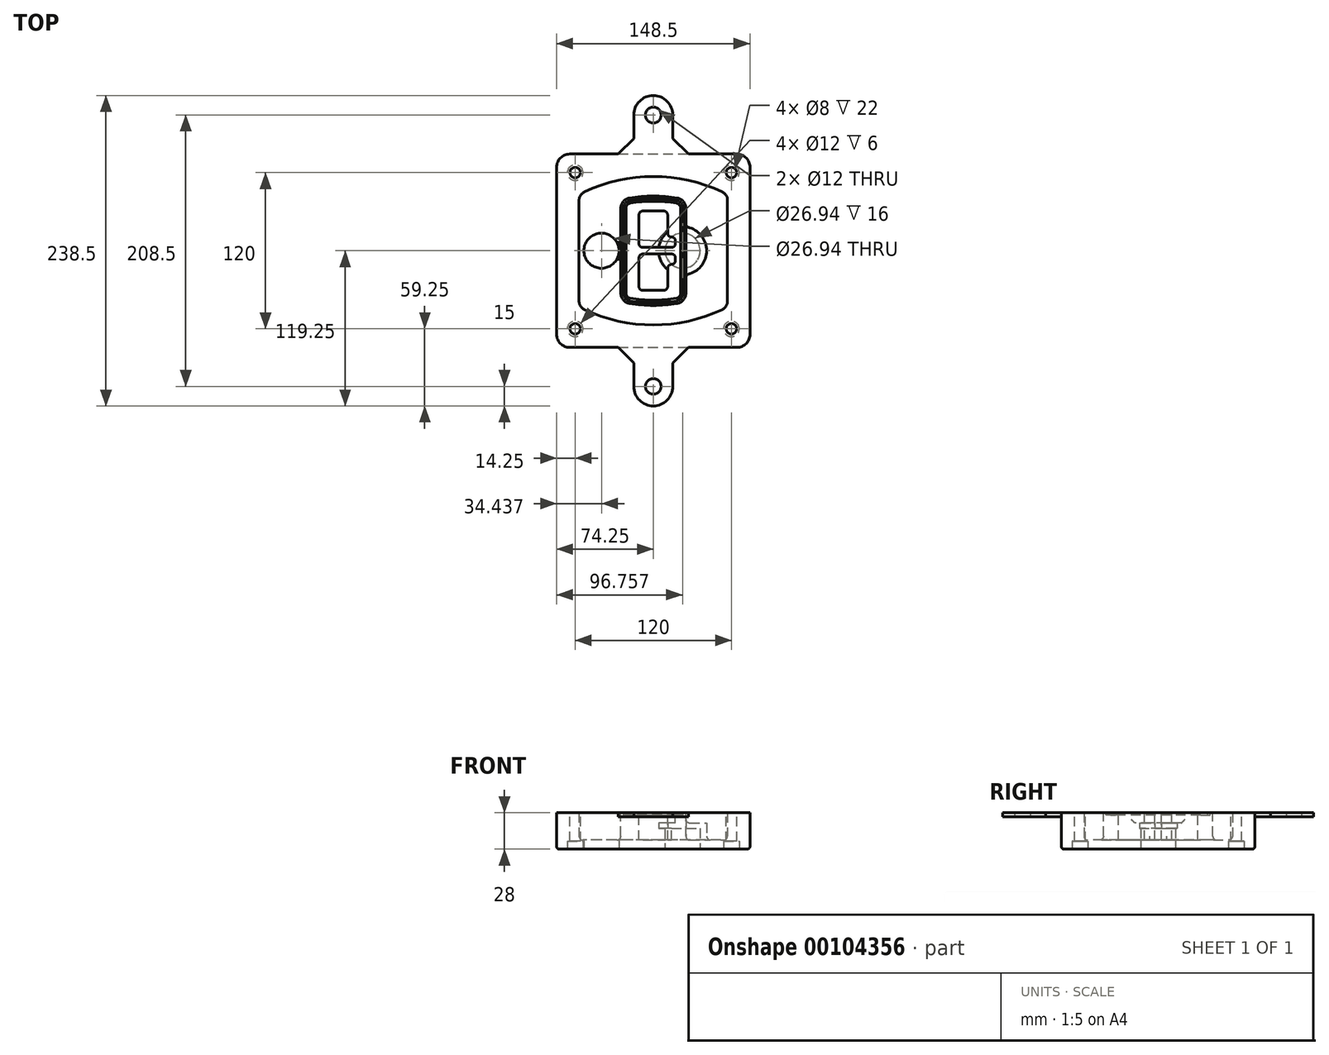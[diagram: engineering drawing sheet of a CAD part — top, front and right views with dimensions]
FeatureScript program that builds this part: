
annotation { "Feature Type Name" : "Feature", "Feature Type Description" : "" }
export const myFeature = defineFeature(function(context is Context, id is Id, definition is map)
    precondition{}
    {
        {
            var Q0;
            Q0=qCreatedBy(makeId("Top.planeOp"),FACE);
            var sketch = newSketch(context, id + "F0", { "sketchPlane" : qUnion([Q0])});
            skPoint(sketch, "E0.rect.middle", {"position": v(0, 0) * mm});
            skLineSegment(sketch, "E1.bottom", {"start": v(-64.25, -74.25) * mm, "end": v(64.25, -74.25) * mm});
            skLineSegment(sketch, "E1.top", {"start": v(-64.25, 74.25) * mm, "end": v(64.25, 74.25) * mm});
            skLineSegment(sketch, "E1.left", {"start": v(-74.25, -64.25) * mm, "end": v(-74.25, 64.25) * mm});
            skLineSegment(sketch, "E1.right", {"start": v(74.25, -64.25) * mm, "end": v(74.25, 64.25) * mm});
            skLineSegment(sketch, "E2", {"start": v(-74.25, 74.25) * mm, "end": v(74.25, -74.25) * mm, "construction": true});
            skLineSegment(sketch, "E3", {"start": v(74.25, 74.25) * mm, "end": v(-74.25, -74.25) * mm, "construction": true});
            skCircle(sketch, "E4", {"center": v(-60, 60) * mm, "radius": 4 * mm});
            skCircle(sketch, "E5", {"center": v(60, 60) * mm, "radius": 4 * mm});
            skCircle(sketch, "E6", {"center": v(60, -60) * mm, "radius": 4 * mm});
            skCircle(sketch, "E7", {"center": v(-60, -60) * mm, "radius": 4 * mm});
            skLineSegment(sketch, "E8", {"start": v(-60, 60) * mm, "end": v(60, 60) * mm, "construction": true});
            skLineSegment(sketch, "E9", {"start": v(60, 60) * mm, "end": v(60, -60) * mm, "construction": true});
            skLineSegment(sketch, "E10", {"start": v(60, -60) * mm, "end": v(-60, -60) * mm, "construction": true});
            skLineSegment(sketch, "E11", {"start": v(-60, -60) * mm, "end": v(-60, 60) * mm, "construction": true});
            skLineSegment(sketch, "E12", {"start": v(-60, 38.83) * mm, "end": v(-60, -38.83) * mm});
            skLineSegment(sketch, "E13", {"start": v(60, 38.83) * mm, "end": v(60, -38.83) * mm});
            skArc(sketch, "E14", {"start": v(54.26, 47.88) * mm, "mid": v(0, 60) * mm, "end": v(-54.26, 47.88) * mm});
            skArc(sketch, "E15", {"start": v(-54.26, -47.88) * mm, "mid": v(0, -60) * mm, "end": v(54.26, -47.88) * mm});
            skLineSegment(sketch, "E16", {"start": v(-60, 0) * mm, "end": v(60, 0) * mm, "construction": true});
            skPoint(sketch, "E17.visualSharp", {"position": v(-60, -45) * mm});
            skArc(sketch, "E17.filletArc", {"start": v(-60, -38.83) * mm, "mid": v(-58.44, -44.2) * mm, "end": v(-54.26, -47.88) * mm});
            skPoint(sketch, "E18.visualSharp", {"position": v(-60, 45) * mm});
            skArc(sketch, "E18.filletArc", {"start": v(-54.26, 47.88) * mm, "mid": v(-58.44, 44.2) * mm, "end": v(-60, 38.83) * mm});
            skPoint(sketch, "E19.visualSharp", {"position": v(60, 45) * mm});
            skArc(sketch, "E19.filletArc", {"start": v(60, 38.83) * mm, "mid": v(58.44, 44.2) * mm, "end": v(54.26, 47.88) * mm});
            skPoint(sketch, "E20.visualSharp", {"position": v(60, -45) * mm});
            skArc(sketch, "E20.filletArc", {"start": v(54.26, -47.88) * mm, "mid": v(58.44, -44.2) * mm, "end": v(60, -38.83) * mm});
            skPoint(sketch, "E21.visualSharp", {"position": v(-74.25, 74.25) * mm});
            skArc(sketch, "E21.filletArc", {"start": v(-64.25, 74.25) * mm, "mid": v(-71.32, 71.32) * mm, "end": v(-74.25, 64.25) * mm});
            skPoint(sketch, "E22.visualSharp", {"position": v(74.25, 74.25) * mm});
            skArc(sketch, "E22.filletArc", {"start": v(74.25, 64.25) * mm, "mid": v(71.32, 71.32) * mm, "end": v(64.25, 74.25) * mm});
            skPoint(sketch, "E23.visualSharp", {"position": v(74.25, -74.25) * mm});
            skArc(sketch, "E23.filletArc", {"start": v(64.25, -74.25) * mm, "mid": v(71.32, -71.32) * mm, "end": v(74.25, -64.25) * mm});
            skPoint(sketch, "E24.visualSharp", {"position": v(-74.25, -74.25) * mm});
            skArc(sketch, "E24.filletArc", {"start": v(-74.25, -64.25) * mm, "mid": v(-71.32, -71.32) * mm, "end": v(-64.25, -74.25) * mm});
            skArc(sketch, "E25.0", {"start": v(57, 38.83) * mm, "mid": v(55.9, 42.58) * mm, "end": v(52.98, 45.17) * mm});
            skLineSegment(sketch, "E25.1", {"start": v(57, 38.83) * mm, "end": v(57, -38.83) * mm});
            skArc(sketch, "E25.2", {"start": v(52.98, -45.17) * mm, "mid": v(55.9, -42.58) * mm, "end": v(57, -38.83) * mm});
            skArc(sketch, "E25.3", {"start": v(-52.98, -45.17) * mm, "mid": v(0, -57) * mm, "end": v(52.98, -45.17) * mm});
            skArc(sketch, "E25.4", {"start": v(-57, -38.83) * mm, "mid": v(-55.9, -42.58) * mm, "end": v(-52.98, -45.17) * mm});
            skArc(sketch, "E25.5", {"start": v(52.98, 45.17) * mm, "mid": v(0, 57) * mm, "end": v(-52.98, 45.17) * mm});
            skLineSegment(sketch, "E25.6", {"start": v(-57, 38.83) * mm, "end": v(-57, -38.83) * mm});
            skArc(sketch, "E25.7", {"start": v(-52.98, 45.17) * mm, "mid": v(-55.9, 42.58) * mm, "end": v(-57, 38.83) * mm});
            skArc(sketch, "E26.0", {"start": v(-55.96, 51.5) * mm, "mid": v(-61.82, 46.33) * mm, "end": v(-64, 38.83) * mm});
            skArc(sketch, "E26.1", {"start": v(55.96, 51.5) * mm, "mid": v(0, 64) * mm, "end": v(-55.96, 51.5) * mm});
            skArc(sketch, "E26.2", {"start": v(64, 38.83) * mm, "mid": v(61.82, 46.33) * mm, "end": v(55.96, 51.5) * mm});
            skLineSegment(sketch, "E26.3", {"start": v(64, 38.83) * mm, "end": v(64, -38.83) * mm});
            skArc(sketch, "E26.4", {"start": v(55.96, -51.5) * mm, "mid": v(61.82, -46.33) * mm, "end": v(64, -38.83) * mm});
            skLineSegment(sketch, "E26.5", {"start": v(-64, 38.83) * mm, "end": v(-64, -38.83) * mm});
            skArc(sketch, "E26.6", {"start": v(-55.96, -51.5) * mm, "mid": v(0, -64) * mm, "end": v(55.96, -51.5) * mm});
            skArc(sketch, "E26.7", {"start": v(-64, -38.83) * mm, "mid": v(-61.82, -46.33) * mm, "end": v(-55.96, -51.5) * mm});
            skSolve(sketch);
        }
        {
            var Q0;
            Q0=makeQuery(id+"F0.imprint","IMPRINT",FACE,{"disambiguationData":[TD([[makeQuery(id+"F0.imprint","IMPRINT",EDGE,{"derivedFrom":sQuery(id+"F0.wireOp",EDGE,"E1.bottom")}),1.0]])]});
            var Q1;
            Q1=makeQuery(id+"F0.imprint","IMPRINT",FACE,{"disambiguationData":[TD([[makeQuery(id+"F0.imprint","IMPRINT",EDGE,{"derivedFrom":sQuery(id+"F0.wireOp",EDGE,"E12")}),1.0]])]});
            var Q2;
            Q2=makeQuery(id+"F0.imprint","IMPRINT",FACE,{"disambiguationData":[TD([[makeQuery(id+"F0.imprint","IMPRINT",EDGE,{"derivedFrom":sQuery(id+"F0.wireOp",EDGE,"E25.0")}),1.0]])]});
            var Q3;
            Q3=makeQuery(id+"F0.imprint","IMPRINT",FACE,{"disambiguationData":[TD([[makeQuery(id+"F0.imprint","IMPRINT",EDGE,{"derivedFrom":sQuery(id+"F0.wireOp",EDGE,"E12")}),-1.0]])]});
            extrude(context, id + "F1", {"entities" : qUnion([Q0, Q1, Q2, Q3]), "oppositeDirection" : true, "depth" : 25 * mm});
        }
        {
            var Q0;
            Q0=makeQuery(id+"F0.imprint","IMPRINT",FACE,{"disambiguationData":[TD([[makeQuery(id+"F0.imprint","IMPRINT",EDGE,{"derivedFrom":sQuery(id+"F0.wireOp",EDGE,"E12")}),1.0]])]});
            extrude(context, id + "F2", {"entities" : qUnion([Q0]), "operationType" : NewBodyOperationType.ADD, "depth" : 3 * mm});
        }
        {
            var Q0;
            Q0=makeQuery(id+"F0.imprint","IMPRINT",FACE,{"disambiguationData":[TD([[makeQuery(id+"F0.imprint","IMPRINT",EDGE,{"derivedFrom":sQuery(id+"F0.wireOp",EDGE,"E25.0")}),1.0]])]});
            extrude(context, id + "F3", {"entities" : qUnion([Q0]), "operationType" : NewBodyOperationType.REMOVE, "oppositeDirection" : true, "depth" : 18 * mm});
        }
        {
            var Q0;
            Q0=makeQuery(id+"F2.opExtrude","CAP_FACE",FACE,{"disambiguationData":[OSD([sQuery(id+"F0.wireOp",EDGE,"E12"),sQuery(id+"F0.wireOp",EDGE,"E13"),sQuery(id+"F0.wireOp",EDGE,"E14"),sQuery(id+"F0.wireOp",EDGE,"E15"),sQuery(id+"F0.wireOp",EDGE,"E17.filletArc"),sQuery(id+"F0.wireOp",EDGE,"E18.filletArc"),sQuery(id+"F0.wireOp",EDGE,"E19.filletArc"),sQuery(id+"F0.wireOp",EDGE,"E20.filletArc"),sQuery(id+"F0.wireOp",EDGE,"E25.0"),sQuery(id+"F0.wireOp",EDGE,"E25.1"),sQuery(id+"F0.wireOp",EDGE,"E25.2"),sQuery(id+"F0.wireOp",EDGE,"E25.3"),sQuery(id+"F0.wireOp",EDGE,"E25.4"),sQuery(id+"F0.wireOp",EDGE,"E25.5"),sQuery(id+"F0.wireOp",EDGE,"E25.6"),sQuery(id+"F0.wireOp",EDGE,"E25.7")])],"isStart":false});
            var sketch = newSketch(context, id + "F4", { "sketchPlane" : qUnion([Q0])});
            skArc(sketch, "E27.0", {"start": v(-18.34, -40.45) * mm, "mid": v(0, -42) * mm, "end": v(18.34, -40.45) * mm});
            skArc(sketch, "E28.0", {"start": v(18.34, 40.45) * mm, "mid": v(0, 42) * mm, "end": v(-18.34, 40.45) * mm});
            skLineSegment(sketch, "E29", {"start": v(-25, 32.57) * mm, "end": v(-25, -32.57) * mm});
            skLineSegment(sketch, "E30", {"start": v(25, 32.57) * mm, "end": v(25, -32.57) * mm});
            skLineSegment(sketch, "E31", {"start": v(-25, 39.1) * mm, "end": v(25, 39.1) * mm, "construction": true});
            skLineSegment(sketch, "E32", {"start": v(-25, -39.1) * mm, "end": v(25, -39.1) * mm, "construction": true});
            skPoint(sketch, "E33.visualSharp", {"position": v(-25, 39.1) * mm});
            skArc(sketch, "E33.filletArc", {"start": v(-18.34, 40.45) * mm, "mid": v(-23.11, 37.73) * mm, "end": v(-25, 32.57) * mm});
            skPoint(sketch, "E34.visualSharp", {"position": v(25, 39.1) * mm});
            skArc(sketch, "E34.filletArc", {"start": v(25, 32.57) * mm, "mid": v(23.11, 37.73) * mm, "end": v(18.34, 40.45) * mm});
            skPoint(sketch, "E35.visualSharp", {"position": v(25, -39.1) * mm});
            skArc(sketch, "E35.filletArc", {"start": v(18.34, -40.45) * mm, "mid": v(23.11, -37.73) * mm, "end": v(25, -32.57) * mm});
            skPoint(sketch, "E36.visualSharp", {"position": v(-25, -39.1) * mm});
            skArc(sketch, "E36.filletArc", {"start": v(-25, -32.57) * mm, "mid": v(-23.11, -37.73) * mm, "end": v(-18.34, -40.45) * mm});
            skArc(sketch, "E37.0", {"start": v(52.98, 45.17) * mm, "mid": v(0, 57) * mm, "end": v(-52.98, 45.17) * mm});
            skArc(sketch, "E37.1", {"start": v(-52.98, 45.17) * mm, "mid": v(-55.9, 42.58) * mm, "end": v(-57, 38.83) * mm});
            skLineSegment(sketch, "E37.2", {"start": v(-57, 38.83) * mm, "end": v(-57, -38.83) * mm});
            skArc(sketch, "E37.3", {"start": v(-57, -38.83) * mm, "mid": v(-55.9, -42.58) * mm, "end": v(-52.98, -45.17) * mm});
            skArc(sketch, "E37.4", {"start": v(-52.98, -45.17) * mm, "mid": v(0, -57) * mm, "end": v(52.98, -45.17) * mm});
            skArc(sketch, "E37.5", {"start": v(52.98, -45.17) * mm, "mid": v(55.9, -42.58) * mm, "end": v(57, -38.83) * mm});
            skLineSegment(sketch, "E37.6", {"start": v(57, 38.83) * mm, "end": v(57, -38.83) * mm});
            skArc(sketch, "E37.7", {"start": v(57, 38.83) * mm, "mid": v(55.9, 42.58) * mm, "end": v(52.98, 45.17) * mm});
            skLineSegment(sketch, "E38.0", {"start": v(23, 32.57) * mm, "end": v(23, -32.57) * mm});
            skArc(sketch, "E38.1", {"start": v(18, -38.48) * mm, "mid": v(21.58, -36.44) * mm, "end": v(23, -32.57) * mm});
            skArc(sketch, "E38.2", {"start": v(-18, -38.48) * mm, "mid": v(0, -40) * mm, "end": v(18, -38.48) * mm});
            skArc(sketch, "E38.3", {"start": v(-23, -32.57) * mm, "mid": v(-21.58, -36.44) * mm, "end": v(-18, -38.48) * mm});
            skLineSegment(sketch, "E38.4", {"start": v(-23, 32.57) * mm, "end": v(-23, -32.57) * mm});
            skArc(sketch, "E38.5", {"start": v(23, 32.57) * mm, "mid": v(21.58, 36.44) * mm, "end": v(18, 38.48) * mm});
            skArc(sketch, "E38.6", {"start": v(-18, 38.48) * mm, "mid": v(-21.58, 36.44) * mm, "end": v(-23, 32.57) * mm});
            skArc(sketch, "E38.7", {"start": v(18, 38.48) * mm, "mid": v(0, 40) * mm, "end": v(-18, 38.48) * mm});
            skArc(sketch, "E39.0", {"start": v(21, 32.57) * mm, "mid": v(20.06, 35.15) * mm, "end": v(17.67, 36.5) * mm});
            skLineSegment(sketch, "E39.1", {"start": v(21, 32.57) * mm, "end": v(21, -32.57) * mm});
            skArc(sketch, "E39.2", {"start": v(17.67, -36.5) * mm, "mid": v(20.06, -35.15) * mm, "end": v(21, -32.57) * mm});
            skArc(sketch, "E39.3", {"start": v(-17.67, -36.5) * mm, "mid": v(0, -38) * mm, "end": v(17.67, -36.5) * mm});
            skArc(sketch, "E39.4", {"start": v(-21, -32.57) * mm, "mid": v(-20.06, -35.15) * mm, "end": v(-17.67, -36.5) * mm});
            skArc(sketch, "E39.5", {"start": v(17.67, 36.5) * mm, "mid": v(0, 38) * mm, "end": v(-17.67, 36.5) * mm});
            skLineSegment(sketch, "E39.6", {"start": v(-21, 32.57) * mm, "end": v(-21, -32.57) * mm});
            skArc(sketch, "E39.7", {"start": v(-17.67, 36.5) * mm, "mid": v(-20.06, 35.15) * mm, "end": v(-21, 32.57) * mm});
            skLineSegment(sketch, "E40", {"start": v(-25, 0) * mm, "end": v(25, 0) * mm, "construction": true});
            skLineSegment(sketch, "E41", {"start": v(-11, 5.5) * mm, "end": v(-11, 27.5) * mm});
            skLineSegment(sketch, "E42", {"start": v(-8, 30.5) * mm, "end": v(8, 30.5) * mm});
            skLineSegment(sketch, "E43", {"start": v(11, 27.5) * mm, "end": v(11, 13.5) * mm});
            skLineSegment(sketch, "E44", {"start": v(14, 10.5) * mm, "end": v(14, 10.5) * mm});
            skLineSegment(sketch, "E45", {"start": v(17, 7.5) * mm, "end": v(17, 5.5) * mm});
            skLineSegment(sketch, "E46", {"start": v(14, 2.5) * mm, "end": v(-8, 2.5) * mm});
            skPoint(sketch, "E47.visualSharp", {"position": v(-11, 30.5) * mm});
            skArc(sketch, "E47.filletArc", {"start": v(-8, 30.5) * mm, "mid": v(-10.12, 29.62) * mm, "end": v(-11, 27.5) * mm});
            skPoint(sketch, "E48.visualSharp", {"position": v(11, 30.5) * mm});
            skArc(sketch, "E48.filletArc", {"start": v(11, 27.5) * mm, "mid": v(10.12, 29.62) * mm, "end": v(8, 30.5) * mm});
            skPoint(sketch, "E49.visualSharp", {"position": v(11, 10.5) * mm});
            skArc(sketch, "E49.filletArc", {"start": v(11, 13.5) * mm, "mid": v(11.88, 11.38) * mm, "end": v(14, 10.5) * mm});
            skPoint(sketch, "E50.visualSharp", {"position": v(17, 10.5) * mm});
            skArc(sketch, "E50.filletArc", {"start": v(17, 7.5) * mm, "mid": v(16.12, 9.62) * mm, "end": v(14, 10.5) * mm});
            skPoint(sketch, "E51.visualSharp", {"position": v(17, 2.5) * mm});
            skArc(sketch, "E51.filletArc", {"start": v(14, 2.5) * mm, "mid": v(16.12, 3.38) * mm, "end": v(17, 5.5) * mm});
            skPoint(sketch, "E52.visualSharp", {"position": v(-11, 2.5) * mm});
            skArc(sketch, "E52.filletArc", {"start": v(-11, 5.5) * mm, "mid": v(-10.12, 3.38) * mm, "end": v(-8, 2.5) * mm});
            skLineSegment(sketch, "E53.0.MirrorCS", {"start": v(14, -2.5) * mm, "end": v(-8, -2.5) * mm});
            skArc(sketch, "E54.0.MirrorCS", {"start": v(-11, -5.5) * mm, "mid": v(-10.12, -3.38) * mm, "end": v(-8, -2.5) * mm});
            skLineSegment(sketch, "E55.0.MirrorCS", {"start": v(-11, -5.5) * mm, "end": v(-11, -27.5) * mm});
            skArc(sketch, "E56.0.MirrorCS", {"start": v(-8, -30.5) * mm, "mid": v(-10.12, -29.62) * mm, "end": v(-11, -27.5) * mm});
            skLineSegment(sketch, "E57.0.MirrorCS", {"start": v(-8, -30.5) * mm, "end": v(8, -30.5) * mm});
            skArc(sketch, "E58.0.MirrorCS", {"start": v(11, -27.5) * mm, "mid": v(10.12, -29.62) * mm, "end": v(8, -30.5) * mm});
            skLineSegment(sketch, "E59.0.MirrorCS", {"start": v(11, -27.5) * mm, "end": v(11, -13.5) * mm});
            skArc(sketch, "E60.0.MirrorCS", {"start": v(11, -13.5) * mm, "mid": v(11.88, -11.38) * mm, "end": v(14, -10.5) * mm});
            skArc(sketch, "E61.0.MirrorCS", {"start": v(17, -7.5) * mm, "mid": v(16.12, -9.62) * mm, "end": v(14, -10.5) * mm});
            skLineSegment(sketch, "E62.0.MirrorCS", {"start": v(17, -7.5) * mm, "end": v(17, -5.5) * mm});
            skArc(sketch, "E63.0.MirrorCS", {"start": v(14, -2.5) * mm, "mid": v(16.12, -3.38) * mm, "end": v(17, -5.5) * mm});
            skSolve(sketch);
        }
        {
            var Q0;
            Q0=makeQuery(id+"F4.imprint","IMPRINT",FACE,{"disambiguationData":[TD([[makeQuery(id+"F4.imprint","IMPRINT",EDGE,{"derivedFrom":sQuery(id+"F4.wireOp",EDGE,"E27.0")}),1.0]])]});
            var Q1;
            Q1=makeQuery(id+"F4.imprint","IMPRINT",FACE,{"disambiguationData":[TD([[makeQuery(id+"F4.imprint","IMPRINT",EDGE,{"derivedFrom":sQuery(id+"F4.wireOp",EDGE,"E38.0")}),-1.0]])]});
            var Q2;
            Q2=makeQuery(id+"F4.imprint","IMPRINT",FACE,{"disambiguationData":[TD([[makeQuery(id+"F4.imprint","IMPRINT",EDGE,{"derivedFrom":sQuery(id+"F4.wireOp",EDGE,"E39.0")}),1.0]])]});
            extrude(context, id + "F5", {"entities" : qUnion([Q0, Q1, Q2]), "operationType" : NewBodyOperationType.ADD, "endBound" : BoundingType.UP_TO_NEXT, "oppositeDirection" : true, "depth" : 25 * mm});
        }
        {
            var Q0;
            Q0=makeQuery(id+"F4.imprint","IMPRINT",FACE,{"disambiguationData":[TD([[makeQuery(id+"F4.imprint","IMPRINT",EDGE,{"derivedFrom":sQuery(id+"F4.wireOp",EDGE,"E38.0")}),-1.0]])]});
            extrude(context, id + "F6", {"entities" : qUnion([Q0]), "operationType" : NewBodyOperationType.REMOVE, "oppositeDirection" : true, "depth" : 2 * mm});
        }
        {
            var Q0;
            Q0=makeQuery(id+"F1.opExtrude","CAP_FACE",FACE,{"disambiguationData":[OSD([sQuery(id+"F0.wireOp",EDGE,"E1.bottom"),sQuery(id+"F0.wireOp",EDGE,"E1.top"),sQuery(id+"F0.wireOp",EDGE,"E1.left"),sQuery(id+"F0.wireOp",EDGE,"E1.right"),sQuery(id+"F0.wireOp",EDGE,"E4"),sQuery(id+"F0.wireOp",EDGE,"E5"),sQuery(id+"F0.wireOp",EDGE,"E6"),sQuery(id+"F0.wireOp",EDGE,"E7"),sQuery(id+"F0.wireOp",EDGE,"E21.filletArc"),sQuery(id+"F0.wireOp",EDGE,"E22.filletArc"),sQuery(id+"F0.wireOp",EDGE,"E23.filletArc"),sQuery(id+"F0.wireOp",EDGE,"E24.filletArc")])],"isStart":false});
            var sketch = newSketch(context, id + "F7", { "sketchPlane" : qUnion([Q0])});
            skCircle(sketch, "E64", {"center": v(22.5, 0) * mm, "radius": 13.47 * mm});
            skCircle(sketch, "E65", {"center": v(-39.81, 0) * mm, "radius": 13.47 * mm});
            skLineSegment(sketch, "E66", {"start": v(74.25, 0) * mm, "end": v(-74.25, 0) * mm});
            skCircle(sketch, "E67", {"center": v(22.5, 0) * mm, "radius": 18.47 * mm});
            skCircle(sketch, "E68", {"center": v(60, -60) * mm, "radius": 6 * mm});
            skCircle(sketch, "E69", {"center": v(-60, -60) * mm, "radius": 6 * mm});
            skCircle(sketch, "E70", {"center": v(-60, 60) * mm, "radius": 6 * mm});
            skCircle(sketch, "E71", {"center": v(60, 60) * mm, "radius": 6 * mm});
            skSolve(sketch);
        }
        {
            var Q0;
            {var subQ1=sQuery(id+"F7.wireOp",EDGE,"E66");var subQ4=sQuery(id+"F7.wireOp",EDGE,"E64");var subQ6=makeQuery(id+"F7.imprint","INTERSECT",VERTEX,{"disambiguationData":[OD(0.0)],"derivedFrom":[subQ4,subQ1]});Q0=makeQuery(id+"F7.imprint","IMPRINT",FACE,{"disambiguationData":[TD([[makeQuery(id+"F7.imprint","IMPRINT",EDGE,{"disambiguationData":[TD([[subQ6,-1.0]])],"derivedFrom":subQ4}),-1.0]])]});}
            var Q1;
            {var subQ0=sQuery(id+"F7.wireOp",EDGE,"E66");var subQ1=sQuery(id+"F7.wireOp",EDGE,"E64");var subQ3=makeQuery(id+"F7.imprint","INTERSECT",VERTEX,{"disambiguationData":[OD(0.0)],"derivedFrom":[subQ1,subQ0]});Q1=makeQuery(id+"F7.imprint","IMPRINT",FACE,{"disambiguationData":[TD([[makeQuery(id+"F7.imprint","IMPRINT",EDGE,{"disambiguationData":[TD([[subQ3,-1.0]])],"derivedFrom":subQ1}),1.0]])]});}
            var Q2;
            {var subQ0=sQuery(id+"F7.wireOp",EDGE,"E66");var subQ1=sQuery(id+"F7.wireOp",EDGE,"E64");var subQ3=makeQuery(id+"F7.imprint","INTERSECT",VERTEX,{"disambiguationData":[OD(0.0)],"derivedFrom":[subQ1,subQ0]});Q2=makeQuery(id+"F7.imprint","IMPRINT",FACE,{"disambiguationData":[TD([[makeQuery(id+"F7.imprint","IMPRINT",EDGE,{"disambiguationData":[TD([[subQ3,1.0]])],"derivedFrom":subQ1}),1.0]])]});}
            var Q3;
            {var subQ1=sQuery(id+"F7.wireOp",EDGE,"E66");var subQ4=sQuery(id+"F7.wireOp",EDGE,"E64");var subQ6=makeQuery(id+"F7.imprint","INTERSECT",VERTEX,{"disambiguationData":[OD(0.0)],"derivedFrom":[subQ4,subQ1]});Q3=makeQuery(id+"F7.imprint","IMPRINT",FACE,{"disambiguationData":[TD([[makeQuery(id+"F7.imprint","IMPRINT",EDGE,{"disambiguationData":[TD([[subQ6,1.0]])],"derivedFrom":subQ4}),-1.0]])]});}
            extrude(context, id + "F8", {"entities" : qUnion([Q0, Q1, Q2, Q3]), "operationType" : NewBodyOperationType.ADD, "oppositeDirection" : true, "depth" : 20 * mm});
        }
        {
            var Q0;
            {var subQ0=sQuery(id+"F7.wireOp",EDGE,"E66");var subQ1=sQuery(id+"F7.wireOp",EDGE,"E64");var subQ3=makeQuery(id+"F7.imprint","INTERSECT",VERTEX,{"disambiguationData":[OD(0.0)],"derivedFrom":[subQ1,subQ0]});Q0=makeQuery(id+"F7.imprint","IMPRINT",FACE,{"disambiguationData":[TD([[makeQuery(id+"F7.imprint","IMPRINT",EDGE,{"disambiguationData":[TD([[subQ3,-1.0]])],"derivedFrom":subQ1}),1.0]])]});}
            var Q1;
            {var subQ0=sQuery(id+"F7.wireOp",EDGE,"E66");var subQ1=sQuery(id+"F7.wireOp",EDGE,"E64");var subQ3=makeQuery(id+"F7.imprint","INTERSECT",VERTEX,{"disambiguationData":[OD(0.0)],"derivedFrom":[subQ1,subQ0]});Q1=makeQuery(id+"F7.imprint","IMPRINT",FACE,{"disambiguationData":[TD([[makeQuery(id+"F7.imprint","IMPRINT",EDGE,{"disambiguationData":[TD([[subQ3,1.0]])],"derivedFrom":subQ1}),1.0]])]});}
            extrude(context, id + "F9", {"entities" : qUnion([Q0, Q1]), "operationType" : NewBodyOperationType.REMOVE, "oppositeDirection" : true, "depth" : 16 * mm});
        }
        {
            var Q0;
            {var subQ0=sQuery(id+"F7.wireOp",EDGE,"E66");var subQ1=sQuery(id+"F7.wireOp",EDGE,"E65");var subQ3=makeQuery(id+"F7.imprint","INTERSECT",VERTEX,{"disambiguationData":[OD(0.0)],"derivedFrom":[subQ1,subQ0]});Q0=makeQuery(id+"F7.imprint","IMPRINT",FACE,{"disambiguationData":[TD([[makeQuery(id+"F7.imprint","IMPRINT",EDGE,{"disambiguationData":[TD([[subQ3,-1.0]])],"derivedFrom":subQ1}),1.0]])]});}
            var Q1;
            {var subQ0=sQuery(id+"F7.wireOp",EDGE,"E66");var subQ1=sQuery(id+"F7.wireOp",EDGE,"E65");var subQ3=makeQuery(id+"F7.imprint","INTERSECT",VERTEX,{"disambiguationData":[OD(0.0)],"derivedFrom":[subQ1,subQ0]});Q1=makeQuery(id+"F7.imprint","IMPRINT",FACE,{"disambiguationData":[TD([[makeQuery(id+"F7.imprint","IMPRINT",EDGE,{"disambiguationData":[TD([[subQ3,1.0]])],"derivedFrom":subQ1}),1.0]])]});}
            extrude(context, id + "F10", {"entities" : qUnion([Q0, Q1]), "operationType" : NewBodyOperationType.REMOVE, "oppositeDirection" : true, "depth" : 25 * mm});
        }
        {
            var Q0;
            Q0=makeQuery(id+"F7.imprint","IMPRINT",FACE,{"disambiguationData":[TD([[makeQuery(id+"F7.imprint","IMPRINT",EDGE,{"derivedFrom":sQuery(id+"F7.wireOp",EDGE,"E68")}),1.0]])]});
            var Q1;
            Q1=makeQuery(id+"F7.imprint","IMPRINT",FACE,{"disambiguationData":[TD([[makeQuery(id+"F7.imprint","IMPRINT",EDGE,{"derivedFrom":makeQuery(id+"F1.opExtrude","CAP_EDGE",EDGE,{"disambiguationData":[OSD([sQuery(id+"F0.wireOp",EDGE,"E5")])],"isStart":false})}),-1.0]])]});
            var Q2;
            Q2=makeQuery(id+"F7.imprint","IMPRINT",FACE,{"disambiguationData":[TD([[makeQuery(id+"F7.imprint","IMPRINT",EDGE,{"derivedFrom":sQuery(id+"F7.wireOp",EDGE,"E69")}),1.0]])]});
            var Q3;
            Q3=makeQuery(id+"F7.imprint","IMPRINT",FACE,{"disambiguationData":[TD([[makeQuery(id+"F7.imprint","IMPRINT",EDGE,{"derivedFrom":makeQuery(id+"F1.opExtrude","CAP_EDGE",EDGE,{"disambiguationData":[OSD([sQuery(id+"F0.wireOp",EDGE,"E4")])],"isStart":false})}),-1.0]])]});
            var Q4;
            Q4=makeQuery(id+"F7.imprint","IMPRINT",FACE,{"disambiguationData":[TD([[makeQuery(id+"F7.imprint","IMPRINT",EDGE,{"derivedFrom":sQuery(id+"F7.wireOp",EDGE,"E70")}),1.0]])]});
            var Q5;
            Q5=makeQuery(id+"F7.imprint","IMPRINT",FACE,{"disambiguationData":[TD([[makeQuery(id+"F7.imprint","IMPRINT",EDGE,{"derivedFrom":makeQuery(id+"F1.opExtrude","CAP_EDGE",EDGE,{"disambiguationData":[OSD([sQuery(id+"F0.wireOp",EDGE,"E7")])],"isStart":false})}),-1.0]])]});
            var Q6;
            Q6=makeQuery(id+"F7.imprint","IMPRINT",FACE,{"disambiguationData":[TD([[makeQuery(id+"F7.imprint","IMPRINT",EDGE,{"derivedFrom":sQuery(id+"F7.wireOp",EDGE,"E71")}),1.0]])]});
            var Q7;
            Q7=makeQuery(id+"F7.imprint","IMPRINT",FACE,{"disambiguationData":[TD([[makeQuery(id+"F7.imprint","IMPRINT",EDGE,{"derivedFrom":makeQuery(id+"F1.opExtrude","CAP_EDGE",EDGE,{"disambiguationData":[OSD([sQuery(id+"F0.wireOp",EDGE,"E6")])],"isStart":false})}),-1.0]])]});
            extrude(context, id + "F11", {"entities" : qUnion([Q0, Q1, Q2, Q3, Q4, Q5, Q6, Q7]), "operationType" : NewBodyOperationType.REMOVE, "oppositeDirection" : true, "depth" : 6 * mm});
        }
        {
            var Q0;
            Q0=makeQuery(id+"F9.boolean.opBoolean","COPY",FACE,{"derivedFrom":makeQuery(id+"F9.opExtrude","CAP_FACE",FACE,{"disambiguationData":[OSD([sQuery(id+"F7.wireOp",EDGE,"E64")])],"isStart":false})});
            var sketch = newSketch(context, id + "F12", { "sketchPlane" : qUnion([Q0])});
            skArc(sketch, "E72.0", {"start": v(11, 14.45) * mm, "mid": v(6.45, 9.13) * mm, "end": v(4.2, 2.5) * mm});
            skArc(sketch, "E72.1", {"start": v(4.2, -2.5) * mm, "mid": v(6.45, -9.13) * mm, "end": v(11, -14.45) * mm});
            skLineSegment(sketch, "E73", {"start": v(4.2, -2.5) * mm, "end": v(14, -2.5) * mm});
            skLineSegment(sketch, "E74.0", {"start": v(14, 2.5) * mm, "end": v(4.2, 2.5) * mm});
            skArc(sketch, "E74.1", {"start": v(14, 2.5) * mm, "mid": v(16.12, 3.38) * mm, "end": v(17, 5.5) * mm});
            skLineSegment(sketch, "E74.2", {"start": v(17, 7.5) * mm, "end": v(17, 5.5) * mm});
            skArc(sketch, "E74.3", {"start": v(17, 7.5) * mm, "mid": v(16.12, 9.62) * mm, "end": v(14, 10.5) * mm});
            skArc(sketch, "E74.4", {"start": v(11, 13.5) * mm, "mid": v(11.88, 11.38) * mm, "end": v(14, 10.5) * mm});
            skLineSegment(sketch, "E74.5", {"start": v(11, 14.45) * mm, "end": v(11, 13.5) * mm});
            skLineSegment(sketch, "E74.7", {"start": v(14, -2.5) * mm, "end": v(4.2, -2.5) * mm});
            skArc(sketch, "E74.8", {"start": v(14, -2.5) * mm, "mid": v(16.12, -3.38) * mm, "end": v(17, -5.5) * mm});
            skLineSegment(sketch, "E74.9", {"start": v(17, -7.5) * mm, "end": v(17, -5.5) * mm});
            skArc(sketch, "E74.10", {"start": v(17, -7.5) * mm, "mid": v(16.12, -9.62) * mm, "end": v(14, -10.5) * mm});
            skArc(sketch, "E74.11", {"start": v(11, -13.5) * mm, "mid": v(11.88, -11.38) * mm, "end": v(14, -10.5) * mm});
            skLineSegment(sketch, "E74.12", {"start": v(11, -14.45) * mm, "end": v(11, -13.5) * mm});
            skPoint(sketch, "E75.orphan", {"position": v(11, -27.5) * mm});
            skPoint(sketch, "E76.orphan", {"position": v(-8, -2.5) * mm});
            skPoint(sketch, "E77.orphan", {"position": v(-8, 2.5) * mm});
            skPoint(sketch, "E78.orphan", {"position": v(11, 27.5) * mm});
            skSolve(sketch);
        }
        {
            var Q0;
            {var subQ7=sQuery(id+"F12.wireOp",EDGE,"E72.0");var subQ14=sQuery(id+"F12.wireOp",EDGE,"E72.1");var subQ16=sQuery(id+"F12.wireOp",EDGE,"E74.1");var subQ18=sQuery(id+"F12.wireOp",EDGE,"E74.8");Q0=qUnion([makeQuery(id+"F12.imprint","IMPRINT",FACE,{"disambiguationData":[TD([[makeQuery(id+"F12.imprint","IMPRINT",EDGE,{"derivedFrom":subQ7}),1.0]])]}),makeQuery(id+"F12.imprint","IMPRINT",FACE,{"disambiguationData":[TD([[makeQuery(id+"F12.imprint","IMPRINT",EDGE,{"derivedFrom":subQ14}),1.0]])]}),makeQuery(id+"F12.imprint","IMPRINT",FACE,{"disambiguationData":[TD([[makeQuery(id+"F12.imprint","IMPRINT",EDGE,{"derivedFrom":subQ16}),1.0]])]}),makeQuery(id+"F12.imprint","IMPRINT",FACE,{"disambiguationData":[TD([[makeQuery(id+"F12.imprint","IMPRINT",EDGE,{"derivedFrom":subQ18}),-1.0]])]})]);}
            var Q1;
            Q1=makeQuery(id+"F5.boolean.opBoolean","SPLIT",FACE,{"disambiguationData":[TD([makeQuery(id+"F5.opExtrude","SWEPT_FACE",FACE,{"disambiguationData":[OSD([sQuery(id+"F4.wireOp",EDGE,"E41")])]})])],"derivedFrom":makeQuery(id+"F3.boolean.opBoolean","COPY",FACE,{"derivedFrom":makeQuery(id+"F3.opExtrude","CAP_FACE",FACE,{"disambiguationData":[OSD([sQuery(id+"F0.wireOp",EDGE,"E25.0"),sQuery(id+"F0.wireOp",EDGE,"E25.1"),sQuery(id+"F0.wireOp",EDGE,"E25.2"),sQuery(id+"F0.wireOp",EDGE,"E25.3"),sQuery(id+"F0.wireOp",EDGE,"E25.4"),sQuery(id+"F0.wireOp",EDGE,"E25.5"),sQuery(id+"F0.wireOp",EDGE,"E25.6"),sQuery(id+"F0.wireOp",EDGE,"E25.7")])],"isStart":false})})});
            extrude(context, id + "F13", {"entities" : qUnion([Q0]), "operationType" : NewBodyOperationType.REMOVE, "endBound" : BoundingType.UP_TO_SURFACE, "endBoundEntityFace" : qUnion([Q1]), "depth" : 25 * mm});
        }
        {
            var Q0;
            Q0=makeQuery(id+"F3.boolean.opBoolean","COPY",EDGE,{"derivedFrom":makeQuery(id+"F3.opExtrude","CAP_EDGE",EDGE,{"disambiguationData":[OSD([sQuery(id+"F0.wireOp",EDGE,"E25.6")])],"isStart":false})});
            var Q1;
            Q1=makeQuery(id+"F8.boolean.opBoolean","INTERSECT",EDGE,{"derivedFrom":[makeQuery(id+"F5.opExtrude","SWEPT_FACE",FACE,{"disambiguationData":[OSD([sQuery(id+"F4.wireOp",EDGE,"E30")])]}),makeQuery(id+"F8.opExtrude","CAP_FACE",FACE,{"disambiguationData":[OSD([sQuery(id+"F7.wireOp",EDGE,"E67")])],"isStart":false})]});
            var Q2;
            Q2=makeQuery(id+"F8.boolean.opBoolean","INTERSECT",EDGE,{"disambiguationData":[OD(1.0)],"derivedFrom":[makeQuery(id+"F5.opExtrude","SWEPT_FACE",FACE,{"disambiguationData":[OSD([sQuery(id+"F4.wireOp",EDGE,"E30")])]}),makeQuery(id+"F8.opExtrude","SWEPT_FACE",FACE,{"disambiguationData":[OSD([sQuery(id+"F7.wireOp",EDGE,"E67")])]})]});
            var Q3;
            {var subQ0=sQuery(id+"F4.wireOp",EDGE,"E30");Q3=makeQuery(id+"F8.boolean.opBoolean","SPLIT",EDGE,{"disambiguationData":[TD([makeQuery(id+"F5.opExtrude","SWEPT_FACE",FACE,{"disambiguationData":[OSD([sQuery(id+"F4.wireOp",EDGE,"E35.filletArc")])]})])],"derivedFrom":makeQuery(id+"F5.opExtrude","CAP_EDGE",EDGE,{"disambiguationData":[OSD([subQ0])],"isStart":false})});}
            var Q4;
            {var subQ0=sQuery(id+"F0.wireOp",EDGE,"E25.7");var subQ1=sQuery(id+"F0.wireOp",EDGE,"E25.1");var subQ2=sQuery(id+"F0.wireOp",EDGE,"E25.6");var subQ3=sQuery(id+"F0.wireOp",EDGE,"E25.5");var subQ4=sQuery(id+"F0.wireOp",EDGE,"E25.4");var subQ5=sQuery(id+"F0.wireOp",EDGE,"E25.0");var subQ6=sQuery(id+"F0.wireOp",EDGE,"E25.2");var subQ7=sQuery(id+"F0.wireOp",EDGE,"E25.3");Q4=makeQuery(id+"F8.boolean.opBoolean","INTERSECT",EDGE,{"derivedFrom":[makeQuery(id+"F5.boolean.opBoolean","SPLIT",FACE,{"disambiguationData":[TD([makeQuery(id+"F2.opExtrude","SWEPT_FACE",FACE,{"disambiguationData":[OSD([subQ5])]})])],"derivedFrom":makeQuery(id+"F3.boolean.opBoolean","COPY",FACE,{"derivedFrom":makeQuery(id+"F3.opExtrude","CAP_FACE",FACE,{"disambiguationData":[OSD([subQ5,subQ1,subQ6,subQ7,subQ4,subQ3,subQ2,subQ0])],"isStart":false})})}),makeQuery(id+"F8.opExtrude","SWEPT_FACE",FACE,{"disambiguationData":[OSD([sQuery(id+"F7.wireOp",EDGE,"E67")])]})]});}
            var Q5;
            Q5=makeQuery(id+"F8.boolean.opBoolean","INTERSECT",EDGE,{"disambiguationData":[OD(0.0)],"derivedFrom":[makeQuery(id+"F5.opExtrude","SWEPT_FACE",FACE,{"disambiguationData":[OSD([sQuery(id+"F4.wireOp",EDGE,"E30")])]}),makeQuery(id+"F8.opExtrude","SWEPT_FACE",FACE,{"disambiguationData":[OSD([sQuery(id+"F7.wireOp",EDGE,"E67")])]})]});
            fillet(context, id + "F14", {"entities" : qUnion([Q0, Q1, Q2, Q3, Q4, Q5]), "radius" : 3 * mm, "tangentPropagation" : true, "allowEdgeOverflow" : false});
        }
        {
            var Q0;
            Q0=makeQuery(id+"F1.opExtrude","CAP_EDGE",EDGE,{"disambiguationData":[OSD([sQuery(id+"F0.wireOp",EDGE,"E1.bottom")])],"isStart":false});
            fillet(context, id + "F15", {"entities" : qUnion([Q0]), "radius" : 2 * mm, "tangentPropagation" : true, "allowEdgeOverflow" : false});
        }
        {
            var Q0;
            {var subQ0=sQuery(id+"F0.wireOp",EDGE,"E22.filletArc");var subQ1=sQuery(id+"F0.wireOp",EDGE,"E7");var subQ2=sQuery(id+"F0.wireOp",EDGE,"E6");var subQ3=sQuery(id+"F0.wireOp",EDGE,"E5");var subQ4=sQuery(id+"F0.wireOp",EDGE,"E4");var subQ5=sQuery(id+"F0.wireOp",EDGE,"E1.bottom");var subQ6=sQuery(id+"F0.wireOp",EDGE,"E21.filletArc");var subQ7=sQuery(id+"F0.wireOp",EDGE,"E1.top");var subQ8=sQuery(id+"F0.wireOp",EDGE,"E1.left");var subQ9=sQuery(id+"F0.wireOp",EDGE,"E1.right");var subQ10=sQuery(id+"F0.wireOp",EDGE,"E23.filletArc");var subQ11=sQuery(id+"F0.wireOp",EDGE,"E24.filletArc");Q0=makeQuery(id+"F2.boolean.opBoolean","SPLIT",FACE,{"disambiguationData":[TD([makeQuery(id+"F1.opExtrude","SWEPT_FACE",FACE,{"disambiguationData":[OSD([subQ5])]})])],"derivedFrom":makeQuery(id+"F1.opExtrude","CAP_FACE",FACE,{"disambiguationData":[OSD([subQ5,subQ7,subQ8,subQ9,subQ4,subQ3,subQ2,subQ1,subQ6,subQ0,subQ10,subQ11])],"isStart":true})});}
            var sketch = newSketch(context, id + "F16", { "sketchPlane" : qUnion([Q0])});
            skLineSegment(sketch, "E79", {"start": v(0, 74.25) * mm, "end": v(0, 104.25) * mm, "construction": true});
            skCircle(sketch, "E80", {"center": v(0, 104.25) * mm, "radius": 6 * mm});
            skLineSegment(sketch, "E81", {"start": v(27, 74.25) * mm, "end": v(15, 86.25) * mm});
            skLineSegment(sketch, "E82", {"start": v(-27, 74.25) * mm, "end": v(-15, 86.25) * mm});
            skLineSegment(sketch, "E83", {"start": v(15, 86.25) * mm, "end": v(15, 104.25) * mm});
            skLineSegment(sketch, "E84", {"start": v(-15, 86.25) * mm, "end": v(-15, 104.25) * mm});
            skArc(sketch, "E85", {"start": v(15, 104.25) * mm, "mid": v(0, 119.25) * mm, "end": v(-15, 104.25) * mm});
            skLineSegment(sketch, "E86", {"start": v(-74.25, 0) * mm, "end": v(74.25, 0) * mm, "construction": true});
            skLineSegment(sketch, "E87.MirrorCS", {"start": v(27, -74.25) * mm, "end": v(15, -86.25) * mm});
            skLineSegment(sketch, "E88.MirrorCS", {"start": v(15, -86.25) * mm, "end": v(15, -104.25) * mm});
            skArc(sketch, "E89.MirrorCS", {"start": v(15, -104.25) * mm, "mid": v(0, -119.25) * mm, "end": v(-15, -104.25) * mm});
            skCircle(sketch, "E90.MirrorC", {"center": v(0, -104.25) * mm, "radius": 6 * mm});
            skLineSegment(sketch, "E91.MirrorCS", {"start": v(-27, -74.25) * mm, "end": v(-15, -86.25) * mm});
            skLineSegment(sketch, "E92.MirrorCS", {"start": v(-15, -86.25) * mm, "end": v(-15, -104.25) * mm});
            skSolve(sketch);
        }
        {
            var Q0;
            Q0=makeQuery(id+"F16.imprint","IMPRINT",FACE,{"disambiguationData":[TD([[makeQuery(id+"F16.imprint","IMPRINT",EDGE,{"derivedFrom":makeQuery(id+"F1.opExtrude","CAP_EDGE",EDGE,{"disambiguationData":[OSD([sQuery(id+"F0.wireOp",EDGE,"E1.left")])],"isStart":true})}),-1.0]])]});
            var Q1;
            Q1=makeQuery(id+"F16.imprint","IMPRINT",FACE,{"disambiguationData":[TD([[makeQuery(id+"F16.imprint","IMPRINT",EDGE,{"derivedFrom":sQuery(id+"F16.wireOp",EDGE,"E80")}),-1.0]])]});
            var Q2;
            {var subQ0=sQuery(id+"F16.wireOp",EDGE,"E87.MirrorCS");Q2=makeQuery(id+"F16.imprint","IMPRINT",FACE,{"disambiguationData":[TD([[makeQuery(id+"F16.imprint","IMPRINT",EDGE,{"derivedFrom":subQ0}),-1.0]])]});}
            var Q3;
            Q3=makeQuery(id+"F2.opExtrude","CAP_FACE",FACE,{"disambiguationData":[OSD([sQuery(id+"F0.wireOp",EDGE,"E12"),sQuery(id+"F0.wireOp",EDGE,"E13"),sQuery(id+"F0.wireOp",EDGE,"E14"),sQuery(id+"F0.wireOp",EDGE,"E15"),sQuery(id+"F0.wireOp",EDGE,"E17.filletArc"),sQuery(id+"F0.wireOp",EDGE,"E18.filletArc"),sQuery(id+"F0.wireOp",EDGE,"E19.filletArc"),sQuery(id+"F0.wireOp",EDGE,"E20.filletArc"),sQuery(id+"F0.wireOp",EDGE,"E25.0"),sQuery(id+"F0.wireOp",EDGE,"E25.1"),sQuery(id+"F0.wireOp",EDGE,"E25.2"),sQuery(id+"F0.wireOp",EDGE,"E25.3"),sQuery(id+"F0.wireOp",EDGE,"E25.4"),sQuery(id+"F0.wireOp",EDGE,"E25.5"),sQuery(id+"F0.wireOp",EDGE,"E25.6"),sQuery(id+"F0.wireOp",EDGE,"E25.7")])],"isStart":false});
            extrude(context, id + "F17", {"entities" : qUnion([Q0, Q1, Q2]), "operationType" : NewBodyOperationType.ADD, "endBound" : BoundingType.UP_TO_SURFACE, "endBoundEntityFace" : qUnion([Q3]), "depth" : 25 * mm});
        }
    });
